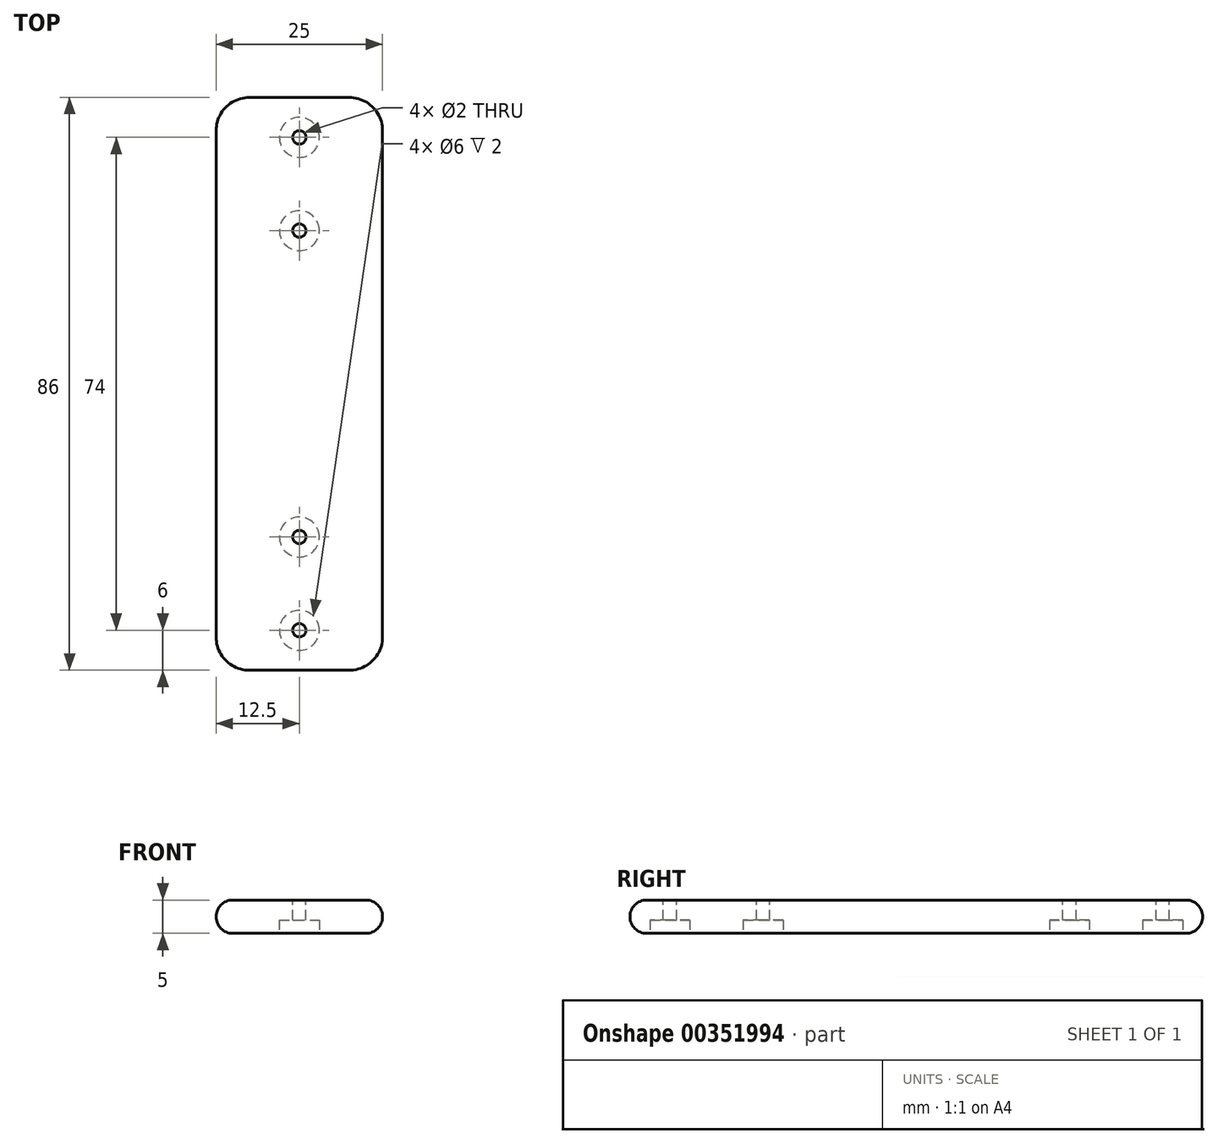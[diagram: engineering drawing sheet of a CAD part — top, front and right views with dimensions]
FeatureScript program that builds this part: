
annotation { "Feature Type Name" : "Feature", "Feature Type Description" : "" }
export const myFeature = defineFeature(function(context is Context, id is Id, definition is map)
    precondition{}
    {
        {
            var Q0;
            Q0=qCreatedBy(makeId("Top.planeOp"),FACE);
            var sketch = newSketch(context, id + "F0", { "sketchPlane" : qUnion([Q0])});
            skLineSegment(sketch, "E0.top", {"start": v(12.5, 43) * mm, "end": v(-12.5, 43) * mm});
            skLineSegment(sketch, "E0.left", {"start": v(12.5, 0) * mm, "end": v(12.5, 43) * mm});
            skLineSegment(sketch, "E0.right", {"start": v(-12.5, 0) * mm, "end": v(-12.5, 43) * mm});
            skPoint(sketch, "E0.middle", {"position": v(0, 0) * mm});
            skLineSegment(sketch, "E1", {"start": v(-12.5, 0) * mm, "end": v(12.5, 0) * mm});
            skLineSegment(sketch, "E2", {"start": v(0, 0) * mm, "end": v(60.2, 0) * mm, "construction": true});
            skSolve(sketch);
        }
        {
            var Q0;
            Q0 = qSketchRegion(id + "F0", true);
            extrude(context, id + "F1", {"entities" : qUnion([Q0]), "oppositeDirection" : true, "depth" : 5 * mm});
        }
        {
            var Q0;
            Q0=makeQuery(id+"F1.opExtrude","CAP_FACE",FACE,{"disambiguationData":[OSD([sQuery(id+"F0.wireOp",EDGE,"E0.top"),sQuery(id+"F0.wireOp",EDGE,"E0.left"),sQuery(id+"F0.wireOp",EDGE,"E0.right"),sQuery(id+"F0.wireOp",EDGE,"E1")])],"isStart":true});
            var sketch = newSketch(context, id + "F2", { "sketchPlane" : qUnion([Q0])});
            skLineSegment(sketch, "E3", {"start": v(0, 43) * mm, "end": v(0, 0) * mm, "construction": true});
            skCircle(sketch, "E4", {"center": v(0, 37) * mm, "radius": 1 * mm});
            skCircle(sketch, "E5", {"center": v(0, 23) * mm, "radius": 1 * mm});
            skLineSegment(sketch, "E6", {"start": v(-12.5, 30) * mm, "end": v(12.5, 30) * mm, "construction": true});
            skSolve(sketch);
        }
        {
            var Q0;
            Q0 = qSketchRegion(id + "F2", true);
            extrude(context, id + "F3", {"entities" : qUnion([Q0]), "operationType" : NewBodyOperationType.REMOVE, "endBound" : BoundingType.THROUGH_ALL, "oppositeDirection" : true, "depth" : 25 * mm});
        }
        {
            var Q0;
            Q0=makeQuery(id+"F1.opExtrude","SWEPT_EDGE",EDGE,{"disambiguationData":[OSD([sQuery(id+"F0.wireOp",EDGE,"E0.top"),sQuery(id+"F0.wireOp",EDGE,"E0.right")])]});
            var Q1;
            Q1=makeQuery(id+"F1.opExtrude","SWEPT_EDGE",EDGE,{"disambiguationData":[OSD([sQuery(id+"F0.wireOp",EDGE,"E0.top"),sQuery(id+"F0.wireOp",EDGE,"E0.left")])]});
            fillet(context, id + "F4", {"entities" : qUnion([Q0, Q1]), "radius" : 5 * mm, "tangentPropagation" : true, "allowEdgeOverflow" : false});
        }
        {
            var Q0;
            Q0=makeQuery(id+"F1.opExtrude","CAP_EDGE",EDGE,{"disambiguationData":[OSD([sQuery(id+"F0.wireOp",EDGE,"E0.right")])],"isStart":true});
            var Q1;
            Q1=makeQuery(id+"F1.opExtrude","CAP_EDGE",EDGE,{"disambiguationData":[OSD([sQuery(id+"F0.wireOp",EDGE,"E0.right")])],"isStart":false});
            fillet(context, id + "F5", {"entities" : qUnion([Q0, Q1]), "radius" : 2.5 * mm, "tangentPropagation" : true, "allowEdgeOverflow" : false});
        }
        {
            var Q0;
            Q0=makeQuery(id+"F1.opExtrude","CAP_FACE",FACE,{"disambiguationData":[OSD([sQuery(id+"F0.wireOp",EDGE,"E0.top"),sQuery(id+"F0.wireOp",EDGE,"E0.left"),sQuery(id+"F0.wireOp",EDGE,"E0.right"),sQuery(id+"F0.wireOp",EDGE,"E1")])],"isStart":false});
            var sketch = newSketch(context, id + "F6", { "sketchPlane" : qUnion([Q0])});
            skCircle(sketch, "E7", {"center": v(0, -37) * mm, "radius": 3 * mm});
            skCircle(sketch, "E8", {"center": v(0, -23) * mm, "radius": 3 * mm});
            skSolve(sketch);
        }
        {
            var Q0;
            Q0 = qSketchRegion(id + "F6", true);
            extrude(context, id + "F7", {"entities" : qUnion([Q0]), "operationType" : NewBodyOperationType.REMOVE, "oppositeDirection" : true, "depth" : 2 * mm});
        }
        {
            var Q0;
            Q0=makeQuery(id+"F1.opExtrude","SWEPT_BODY",BODY,{"disambiguationData":[OSD([sQuery(id+"F0.wireOp",EDGE,"E0.top"),sQuery(id+"F0.wireOp",EDGE,"E0.left"),sQuery(id+"F0.wireOp",EDGE,"E0.right"),sQuery(id+"F0.wireOp",EDGE,"E1")])]});
            var Q1;
            Q1=qCreatedBy(makeId("Front.planeOp"),FACE);
            mirror(context, id + "F8", {"operationType" : NewBodyOperationType.ADD, "entities" : qUnion([Q0]), "mirrorPlane" : qUnion([Q1])});
        }
    });
